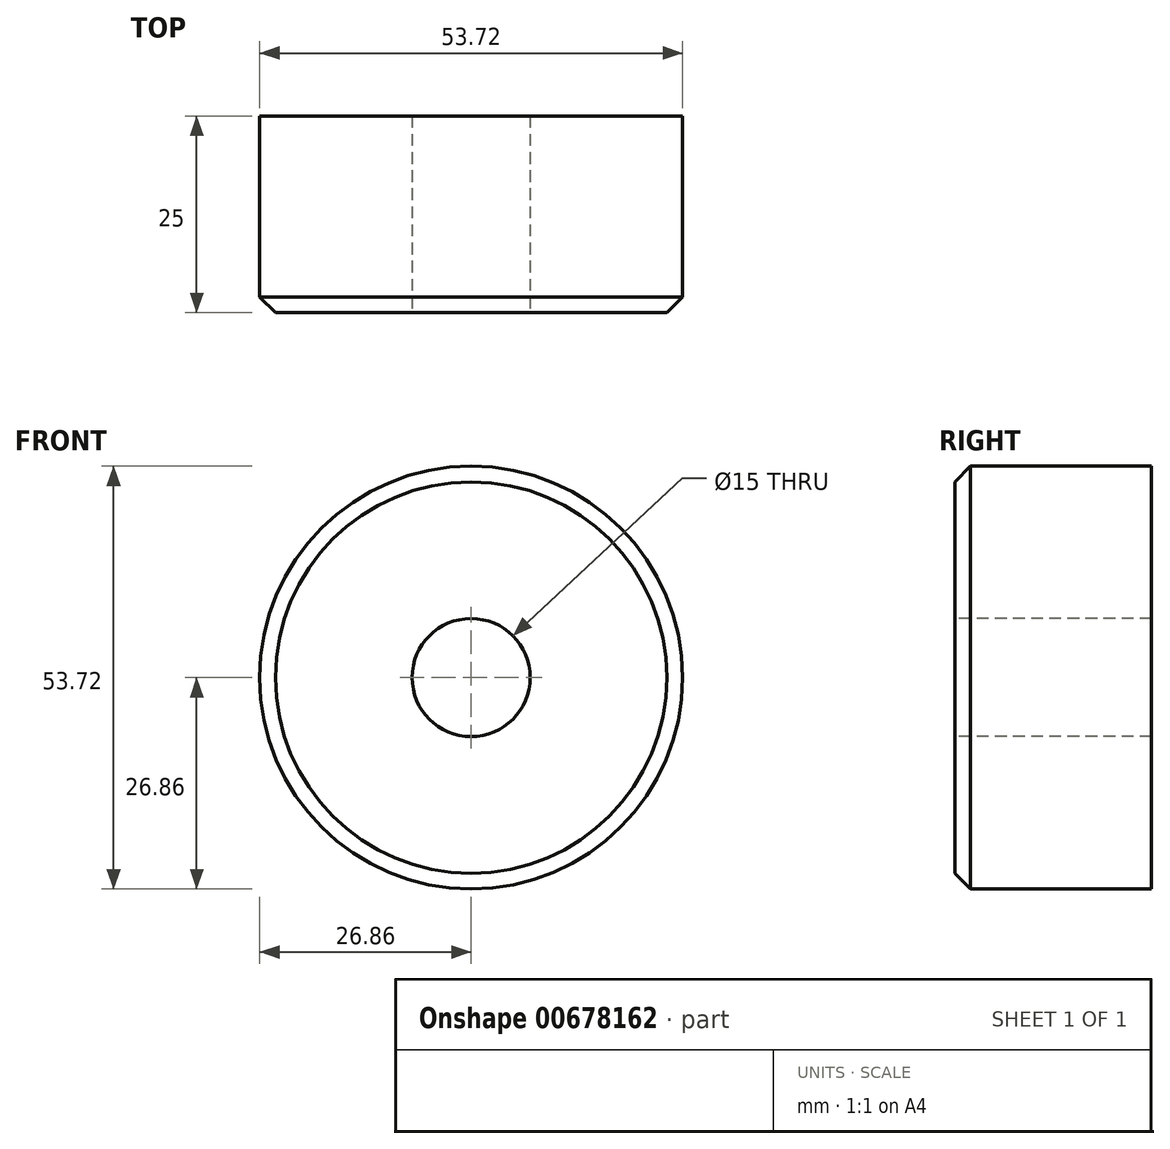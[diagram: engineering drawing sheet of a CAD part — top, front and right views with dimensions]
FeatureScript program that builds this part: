
annotation { "Feature Type Name" : "Feature", "Feature Type Description" : "" }
export const myFeature = defineFeature(function(context is Context, id is Id, definition is map)
    precondition{}
    {
        {
            var Q0;
            Q0=qCreatedBy(makeId("Front.planeOp"),FACE);
            var sketch = newSketch(context, id + "F0", { "sketchPlane" : qUnion([Q0])});
            skCircle(sketch, "E0", {"center": v(0, 0) * mm, "radius": 26.86 * mm});
            skCircle(sketch, "E1", {"center": v(0, 0) * mm, "radius": 27.57 * mm, "construction": true});
            skCircle(sketch, "E2", {"center": v(0, 0) * mm, "radius": 29.34 * mm, "construction": true});
            skCircle(sketch, "E3", {"center": v(0, 0) * mm, "radius": 31.75 * mm, "construction": true});
            skLineSegment(sketch, "E4", {"start": v(0, 37.7) * mm, "end": v(0, 0) * mm, "construction": true});
            skLineSegment(sketch, "E5", {"start": v(0, 0) * mm, "end": v(-2.52, 38.42) * mm, "construction": true});
            skCircle(sketch, "E6", {"center": v(0, 29.34) * mm, "radius": 14.6 * mm, "construction": true});
            skLineSegment(sketch, "E7", {"start": v(0, 29.34) * mm, "end": v(-36.62, 29.34) * mm, "construction": true});
            skLineSegment(sketch, "E8", {"start": v(0, 29.34) * mm, "end": v(-34.85, 16.65) * mm, "construction": true});
            skArc(sketch, "E9.MirrorCS", {"start": v(-6.13, 26.15) * mm, "mid": v(-6.22, 28.64) * mm, "end": v(-5.9, 31.1) * mm});
            skArc(sketch, "E10.MirrorCS", {"start": v(-5.9, 31.1) * mm, "mid": v(-5.03, 33.76) * mm, "end": v(-3.68, 36.2) * mm});
            skArc(sketch, "E11.MirrorCS", {"start": v(1.78, 31.6) * mm, "mid": v(0.58, 34.12) * mm, "end": v(-1.08, 36.37) * mm});
            skArc(sketch, "E12.MirrorCS", {"start": v(2.66, 26.73) * mm, "mid": v(2.43, 29.2) * mm, "end": v(1.78, 31.6) * mm});
            skLineSegment(sketch, "E13", {"start": v(-3.68, 36.2) * mm, "end": v(-1.08, 36.37) * mm});
            skSolve(sketch);
        }
        {
            var Q0;
            {var subQ0=sQuery(id+"F0.wireOp",EDGE,"E0");var subQ1=makeQuery(id+"F0.imprint","INTERSECT",VERTEX,{"derivedFrom":[subQ0,sQuery(id+"F0.wireOp",EDGE,"E9.MirrorCS")]});Q0=makeQuery(id+"F0.imprint","IMPRINT",FACE,{"disambiguationData":[TD([[makeQuery(id+"F0.imprint","IMPRINT",EDGE,{"disambiguationData":[TD([[subQ1,1.0]])],"derivedFrom":subQ0}),1.0]])]});}
            var Q1;
            {var subQ0=sQuery(id+"F0.wireOp",EDGE,"E9.MirrorCS");Q1=makeQuery(id+"F0.imprint","IMPRINT",FACE,{"disambiguationData":[TD([[makeQuery(id+"F0.imprint","IMPRINT",EDGE,{"derivedFrom":subQ0}),-1.0]])]});}
            extrude(context, id + "F1", {"entities" : qUnion([Q0, Q1]), "depth" : 25 * mm, "offsetDistance" : 25 * mm});
        }
        {
            var Q0;
            Q0=makeQuery(id+"F1.opExtrude","SWEPT_BODY",BODY,{"disambiguationData":[OSD([sQuery(id+"F0.wireOp",EDGE,"E0"),sQuery(id+"F0.wireOp",EDGE,"E9.MirrorCS"),sQuery(id+"F0.wireOp",EDGE,"E10.MirrorCS"),sQuery(id+"F0.wireOp",EDGE,"E11.MirrorCS"),sQuery(id+"F0.wireOp",EDGE,"E12.MirrorCS"),sQuery(id+"F0.wireOp",EDGE,"E13")])]});
            var Q1;
            Q1=makeQuery(id+"F1.opExtrude","SWEPT_FACE",FACE,{"disambiguationData":[OSD([sQuery(id+"F0.wireOp",EDGE,"E0")])]});
            circularPattern(context, id + "F2", {"operationType" : NewBodyOperationType.ADD, "entities" : qUnion([Q0]), "axis" : qUnion([Q1]), "angle" : 360 * degree, "instanceCount" : 12, "equalSpace" : true});
        }
        {
            var Q0;
            Q0=makeQuery(id+"F1.opExtrude","CAP_FACE",FACE,{"disambiguationData":[OSD([sQuery(id+"F0.wireOp",EDGE,"E0"),sQuery(id+"F0.wireOp",EDGE,"E9.MirrorCS"),sQuery(id+"F0.wireOp",EDGE,"E10.MirrorCS"),sQuery(id+"F0.wireOp",EDGE,"E11.MirrorCS"),sQuery(id+"F0.wireOp",EDGE,"E12.MirrorCS"),sQuery(id+"F0.wireOp",EDGE,"E13")])],"isStart":false});
            var Q1;
            Q1=makeQuery(id+"F2.opPattern","COPY",FACE,{"derivedFrom":makeQuery(id+"F1.opExtrude","CAP_FACE",FACE,{"disambiguationData":[OSD([sQuery(id+"F0.wireOp",EDGE,"E0"),sQuery(id+"F0.wireOp",EDGE,"E9.MirrorCS"),sQuery(id+"F0.wireOp",EDGE,"E10.MirrorCS"),sQuery(id+"F0.wireOp",EDGE,"E11.MirrorCS"),sQuery(id+"F0.wireOp",EDGE,"E12.MirrorCS"),sQuery(id+"F0.wireOp",EDGE,"E13")])],"isStart":false}),"instanceName":"11"});
            var Q2;
            Q2=makeQuery(id+"F2.opPattern","COPY",FACE,{"derivedFrom":makeQuery(id+"F1.opExtrude","CAP_FACE",FACE,{"disambiguationData":[OSD([sQuery(id+"F0.wireOp",EDGE,"E0"),sQuery(id+"F0.wireOp",EDGE,"E9.MirrorCS"),sQuery(id+"F0.wireOp",EDGE,"E10.MirrorCS"),sQuery(id+"F0.wireOp",EDGE,"E11.MirrorCS"),sQuery(id+"F0.wireOp",EDGE,"E12.MirrorCS"),sQuery(id+"F0.wireOp",EDGE,"E13")])],"isStart":false}),"instanceName":"10"});
            var Q3;
            Q3=makeQuery(id+"F2.opPattern","COPY",FACE,{"derivedFrom":makeQuery(id+"F1.opExtrude","CAP_FACE",FACE,{"disambiguationData":[OSD([sQuery(id+"F0.wireOp",EDGE,"E0"),sQuery(id+"F0.wireOp",EDGE,"E9.MirrorCS"),sQuery(id+"F0.wireOp",EDGE,"E10.MirrorCS"),sQuery(id+"F0.wireOp",EDGE,"E11.MirrorCS"),sQuery(id+"F0.wireOp",EDGE,"E12.MirrorCS"),sQuery(id+"F0.wireOp",EDGE,"E13")])],"isStart":false}),"instanceName":"9"});
            var Q4;
            Q4=makeQuery(id+"F2.opPattern","COPY",FACE,{"derivedFrom":makeQuery(id+"F1.opExtrude","CAP_FACE",FACE,{"disambiguationData":[OSD([sQuery(id+"F0.wireOp",EDGE,"E0"),sQuery(id+"F0.wireOp",EDGE,"E9.MirrorCS"),sQuery(id+"F0.wireOp",EDGE,"E10.MirrorCS"),sQuery(id+"F0.wireOp",EDGE,"E11.MirrorCS"),sQuery(id+"F0.wireOp",EDGE,"E12.MirrorCS"),sQuery(id+"F0.wireOp",EDGE,"E13")])],"isStart":false}),"instanceName":"8"});
            var Q5;
            Q5=makeQuery(id+"F2.opPattern","COPY",FACE,{"derivedFrom":makeQuery(id+"F1.opExtrude","CAP_FACE",FACE,{"disambiguationData":[OSD([sQuery(id+"F0.wireOp",EDGE,"E0"),sQuery(id+"F0.wireOp",EDGE,"E9.MirrorCS"),sQuery(id+"F0.wireOp",EDGE,"E10.MirrorCS"),sQuery(id+"F0.wireOp",EDGE,"E11.MirrorCS"),sQuery(id+"F0.wireOp",EDGE,"E12.MirrorCS"),sQuery(id+"F0.wireOp",EDGE,"E13")])],"isStart":false}),"instanceName":"7"});
            var Q6;
            Q6=makeQuery(id+"F2.opPattern","COPY",FACE,{"derivedFrom":makeQuery(id+"F1.opExtrude","CAP_FACE",FACE,{"disambiguationData":[OSD([sQuery(id+"F0.wireOp",EDGE,"E0"),sQuery(id+"F0.wireOp",EDGE,"E9.MirrorCS"),sQuery(id+"F0.wireOp",EDGE,"E10.MirrorCS"),sQuery(id+"F0.wireOp",EDGE,"E11.MirrorCS"),sQuery(id+"F0.wireOp",EDGE,"E12.MirrorCS"),sQuery(id+"F0.wireOp",EDGE,"E13")])],"isStart":false}),"instanceName":"6"});
            var Q7;
            Q7=makeQuery(id+"F2.opPattern","COPY",FACE,{"derivedFrom":makeQuery(id+"F1.opExtrude","CAP_FACE",FACE,{"disambiguationData":[OSD([sQuery(id+"F0.wireOp",EDGE,"E0"),sQuery(id+"F0.wireOp",EDGE,"E9.MirrorCS"),sQuery(id+"F0.wireOp",EDGE,"E10.MirrorCS"),sQuery(id+"F0.wireOp",EDGE,"E11.MirrorCS"),sQuery(id+"F0.wireOp",EDGE,"E12.MirrorCS"),sQuery(id+"F0.wireOp",EDGE,"E13")])],"isStart":false}),"instanceName":"5"});
            var Q8;
            Q8=makeQuery(id+"F2.opPattern","COPY",FACE,{"derivedFrom":makeQuery(id+"F1.opExtrude","CAP_FACE",FACE,{"disambiguationData":[OSD([sQuery(id+"F0.wireOp",EDGE,"E0"),sQuery(id+"F0.wireOp",EDGE,"E9.MirrorCS"),sQuery(id+"F0.wireOp",EDGE,"E10.MirrorCS"),sQuery(id+"F0.wireOp",EDGE,"E11.MirrorCS"),sQuery(id+"F0.wireOp",EDGE,"E12.MirrorCS"),sQuery(id+"F0.wireOp",EDGE,"E13")])],"isStart":false}),"instanceName":"4"});
            var Q9;
            Q9=makeQuery(id+"F2.opPattern","COPY",FACE,{"derivedFrom":makeQuery(id+"F1.opExtrude","CAP_FACE",FACE,{"disambiguationData":[OSD([sQuery(id+"F0.wireOp",EDGE,"E0"),sQuery(id+"F0.wireOp",EDGE,"E9.MirrorCS"),sQuery(id+"F0.wireOp",EDGE,"E10.MirrorCS"),sQuery(id+"F0.wireOp",EDGE,"E11.MirrorCS"),sQuery(id+"F0.wireOp",EDGE,"E12.MirrorCS"),sQuery(id+"F0.wireOp",EDGE,"E13")])],"isStart":false}),"instanceName":"3"});
            var Q10;
            Q10=makeQuery(id+"F2.opPattern","COPY",FACE,{"derivedFrom":makeQuery(id+"F1.opExtrude","CAP_FACE",FACE,{"disambiguationData":[OSD([sQuery(id+"F0.wireOp",EDGE,"E0"),sQuery(id+"F0.wireOp",EDGE,"E9.MirrorCS"),sQuery(id+"F0.wireOp",EDGE,"E10.MirrorCS"),sQuery(id+"F0.wireOp",EDGE,"E11.MirrorCS"),sQuery(id+"F0.wireOp",EDGE,"E12.MirrorCS"),sQuery(id+"F0.wireOp",EDGE,"E13")])],"isStart":false}),"instanceName":"2"});
            var Q11;
            Q11=makeQuery(id+"F2.opPattern","COPY",FACE,{"derivedFrom":makeQuery(id+"F1.opExtrude","CAP_FACE",FACE,{"disambiguationData":[OSD([sQuery(id+"F0.wireOp",EDGE,"E0"),sQuery(id+"F0.wireOp",EDGE,"E9.MirrorCS"),sQuery(id+"F0.wireOp",EDGE,"E10.MirrorCS"),sQuery(id+"F0.wireOp",EDGE,"E11.MirrorCS"),sQuery(id+"F0.wireOp",EDGE,"E12.MirrorCS"),sQuery(id+"F0.wireOp",EDGE,"E13")])],"isStart":false}),"instanceName":"1"});
            chamfer(context, id + "F3", {"entities" : qUnion([Q0, Q1, Q2, Q3, Q4, Q5, Q6, Q7, Q8, Q9, Q10, Q11]), "width" : 2 * mm, "tangentPropagation" : true});
        }
        {
            var Q0;
            Q0=makeQuery(id+"F1.opExtrude","CAP_FACE",FACE,{"disambiguationData":[OSD([sQuery(id+"F0.wireOp",EDGE,"E0"),sQuery(id+"F0.wireOp",EDGE,"E9.MirrorCS"),sQuery(id+"F0.wireOp",EDGE,"E10.MirrorCS"),sQuery(id+"F0.wireOp",EDGE,"E11.MirrorCS"),sQuery(id+"F0.wireOp",EDGE,"E12.MirrorCS"),sQuery(id+"F0.wireOp",EDGE,"E13")])],"isStart":false});
            var sketch = newSketch(context, id + "F4", { "sketchPlane" : qUnion([Q0])});
            skPoint(sketch, "E14", {"position": v(0, 0) * mm});
            skSolve(sketch);
        }
        {
            var Q0;
            Q0=sQuery(id+"F4.wireOp",VERTEX,"E14");
            var Q1;
            Q1=makeQuery(id+"F1.opExtrude","SWEPT_BODY",BODY,{"disambiguationData":[OSD([sQuery(id+"F0.wireOp",EDGE,"E0"),sQuery(id+"F0.wireOp",EDGE,"E9.MirrorCS"),sQuery(id+"F0.wireOp",EDGE,"E10.MirrorCS"),sQuery(id+"F0.wireOp",EDGE,"E11.MirrorCS"),sQuery(id+"F0.wireOp",EDGE,"E12.MirrorCS"),sQuery(id+"F0.wireOp",EDGE,"E13")])]});
            var Q2;
            Q2=makeQuery(id+"F2.opPattern","COPY",BODY,{"derivedFrom":makeQuery(id+"F1.opExtrude","SWEPT_BODY",BODY,{"disambiguationData":[OSD([sQuery(id+"F0.wireOp",EDGE,"E0"),sQuery(id+"F0.wireOp",EDGE,"E9.MirrorCS"),sQuery(id+"F0.wireOp",EDGE,"E10.MirrorCS"),sQuery(id+"F0.wireOp",EDGE,"E11.MirrorCS"),sQuery(id+"F0.wireOp",EDGE,"E12.MirrorCS"),sQuery(id+"F0.wireOp",EDGE,"E13")])]}),"instanceName":"11"});
            var Q3;
            Q3=makeQuery(id+"F2.opPattern","COPY",BODY,{"derivedFrom":makeQuery(id+"F1.opExtrude","SWEPT_BODY",BODY,{"disambiguationData":[OSD([sQuery(id+"F0.wireOp",EDGE,"E0"),sQuery(id+"F0.wireOp",EDGE,"E9.MirrorCS"),sQuery(id+"F0.wireOp",EDGE,"E10.MirrorCS"),sQuery(id+"F0.wireOp",EDGE,"E11.MirrorCS"),sQuery(id+"F0.wireOp",EDGE,"E12.MirrorCS"),sQuery(id+"F0.wireOp",EDGE,"E13")])]}),"instanceName":"10"});
            var Q4;
            Q4=makeQuery(id+"F2.opPattern","COPY",BODY,{"derivedFrom":makeQuery(id+"F1.opExtrude","SWEPT_BODY",BODY,{"disambiguationData":[OSD([sQuery(id+"F0.wireOp",EDGE,"E0"),sQuery(id+"F0.wireOp",EDGE,"E9.MirrorCS"),sQuery(id+"F0.wireOp",EDGE,"E10.MirrorCS"),sQuery(id+"F0.wireOp",EDGE,"E11.MirrorCS"),sQuery(id+"F0.wireOp",EDGE,"E12.MirrorCS"),sQuery(id+"F0.wireOp",EDGE,"E13")])]}),"instanceName":"9"});
            var Q5;
            Q5=makeQuery(id+"F2.opPattern","COPY",BODY,{"derivedFrom":makeQuery(id+"F1.opExtrude","SWEPT_BODY",BODY,{"disambiguationData":[OSD([sQuery(id+"F0.wireOp",EDGE,"E0"),sQuery(id+"F0.wireOp",EDGE,"E9.MirrorCS"),sQuery(id+"F0.wireOp",EDGE,"E10.MirrorCS"),sQuery(id+"F0.wireOp",EDGE,"E11.MirrorCS"),sQuery(id+"F0.wireOp",EDGE,"E12.MirrorCS"),sQuery(id+"F0.wireOp",EDGE,"E13")])]}),"instanceName":"8"});
            var Q6;
            Q6=makeQuery(id+"F2.opPattern","COPY",BODY,{"derivedFrom":makeQuery(id+"F1.opExtrude","SWEPT_BODY",BODY,{"disambiguationData":[OSD([sQuery(id+"F0.wireOp",EDGE,"E0"),sQuery(id+"F0.wireOp",EDGE,"E9.MirrorCS"),sQuery(id+"F0.wireOp",EDGE,"E10.MirrorCS"),sQuery(id+"F0.wireOp",EDGE,"E11.MirrorCS"),sQuery(id+"F0.wireOp",EDGE,"E12.MirrorCS"),sQuery(id+"F0.wireOp",EDGE,"E13")])]}),"instanceName":"7"});
            var Q7;
            Q7=makeQuery(id+"F2.opPattern","COPY",BODY,{"derivedFrom":makeQuery(id+"F1.opExtrude","SWEPT_BODY",BODY,{"disambiguationData":[OSD([sQuery(id+"F0.wireOp",EDGE,"E0"),sQuery(id+"F0.wireOp",EDGE,"E9.MirrorCS"),sQuery(id+"F0.wireOp",EDGE,"E10.MirrorCS"),sQuery(id+"F0.wireOp",EDGE,"E11.MirrorCS"),sQuery(id+"F0.wireOp",EDGE,"E12.MirrorCS"),sQuery(id+"F0.wireOp",EDGE,"E13")])]}),"instanceName":"6"});
            var Q8;
            Q8=makeQuery(id+"F2.opPattern","COPY",BODY,{"derivedFrom":makeQuery(id+"F1.opExtrude","SWEPT_BODY",BODY,{"disambiguationData":[OSD([sQuery(id+"F0.wireOp",EDGE,"E0"),sQuery(id+"F0.wireOp",EDGE,"E9.MirrorCS"),sQuery(id+"F0.wireOp",EDGE,"E10.MirrorCS"),sQuery(id+"F0.wireOp",EDGE,"E11.MirrorCS"),sQuery(id+"F0.wireOp",EDGE,"E12.MirrorCS"),sQuery(id+"F0.wireOp",EDGE,"E13")])]}),"instanceName":"5"});
            var Q9;
            Q9=makeQuery(id+"F2.opPattern","COPY",BODY,{"derivedFrom":makeQuery(id+"F1.opExtrude","SWEPT_BODY",BODY,{"disambiguationData":[OSD([sQuery(id+"F0.wireOp",EDGE,"E0"),sQuery(id+"F0.wireOp",EDGE,"E9.MirrorCS"),sQuery(id+"F0.wireOp",EDGE,"E10.MirrorCS"),sQuery(id+"F0.wireOp",EDGE,"E11.MirrorCS"),sQuery(id+"F0.wireOp",EDGE,"E12.MirrorCS"),sQuery(id+"F0.wireOp",EDGE,"E13")])]}),"instanceName":"4"});
            var Q10;
            Q10=makeQuery(id+"F2.opPattern","COPY",BODY,{"derivedFrom":makeQuery(id+"F1.opExtrude","SWEPT_BODY",BODY,{"disambiguationData":[OSD([sQuery(id+"F0.wireOp",EDGE,"E0"),sQuery(id+"F0.wireOp",EDGE,"E9.MirrorCS"),sQuery(id+"F0.wireOp",EDGE,"E10.MirrorCS"),sQuery(id+"F0.wireOp",EDGE,"E11.MirrorCS"),sQuery(id+"F0.wireOp",EDGE,"E12.MirrorCS"),sQuery(id+"F0.wireOp",EDGE,"E13")])]}),"instanceName":"3"});
            var Q11;
            Q11=makeQuery(id+"F2.opPattern","COPY",BODY,{"derivedFrom":makeQuery(id+"F1.opExtrude","SWEPT_BODY",BODY,{"disambiguationData":[OSD([sQuery(id+"F0.wireOp",EDGE,"E0"),sQuery(id+"F0.wireOp",EDGE,"E9.MirrorCS"),sQuery(id+"F0.wireOp",EDGE,"E10.MirrorCS"),sQuery(id+"F0.wireOp",EDGE,"E11.MirrorCS"),sQuery(id+"F0.wireOp",EDGE,"E12.MirrorCS"),sQuery(id+"F0.wireOp",EDGE,"E13")])]}),"instanceName":"2"});
            var Q12;
            Q12=makeQuery(id+"F2.opPattern","COPY",BODY,{"derivedFrom":makeQuery(id+"F1.opExtrude","SWEPT_BODY",BODY,{"disambiguationData":[OSD([sQuery(id+"F0.wireOp",EDGE,"E0"),sQuery(id+"F0.wireOp",EDGE,"E9.MirrorCS"),sQuery(id+"F0.wireOp",EDGE,"E10.MirrorCS"),sQuery(id+"F0.wireOp",EDGE,"E11.MirrorCS"),sQuery(id+"F0.wireOp",EDGE,"E12.MirrorCS"),sQuery(id+"F0.wireOp",EDGE,"E13")])]}),"instanceName":"1"});
            hole(context, id + "F5", {"style" : HoleStyle.SIMPLE, "endStyle" : HoleEndStyle.THROUGH, "holeDiameter" : 15 * mm, "majorDiameter" : 5 * mm, "isTappedThrough" : true, "tappedDepth" : 12 * mm, "tapClearance" : 3, "locations" : qUnion([Q0]), "scope" : qUnion([Q1, Q2, Q3, Q4, Q5, Q6, Q7, Q8, Q9, Q10, Q11, Q12])});
        }
    });
